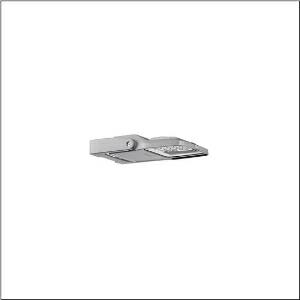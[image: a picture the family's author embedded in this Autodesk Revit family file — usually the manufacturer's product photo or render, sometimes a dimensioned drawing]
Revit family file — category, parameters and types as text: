
# Revit family: floodlight_fl_21_micro___pl64_5xa7761a2e2a_558a
name_source: partatom
category: Lighting Fixtures
units: mm (PartAtom-declared; Revit-internal decimal feet)

## family parameters
Cut with Voids When Loaded = No
Host = Face
Light Source = No
Part Type = Normal
Room Calculation Point = No
Round Connector Dimension = Use Diameter
Shared = No

## types (1)
- --- (1 x LED, 2870 lm, 23.1 W, 3000K)
    Apparent Load = 23 VA
    CIE Flux Codes = 28 80 98 100 100
    Color Rendering = 70
    Color Temperature = 3000K
    Default Elevation = 1800 mm
    Description = Floodlight FL 21 micro, floodlight, primary light control with lens, of PMMA, primary optical cover: protective disc, of toughened safety glass, transparent, light distribution: PL64, light emission: direct distribution, installation type: surface-mounted, LED, High Power LED, rated luminous flux: 2.870lm, luminous efficacy: 124lm/W, light colour: 730, colour temperature: 3000K, control gear: ECG iQ, control: optimised constant luminous flux control (CLO 2.0), Desk-Remote (wireless, voltage-free reading and setting of iQ features in the workshop via application-optimized NFC function/RFID function), Light-Fading, Smart-Wire, Night-Set, Lumen-Switch, Temp-Guard, Auto-Match, with terminal, 6-pole, mains connection: 220..240V, AC, 50/60Hz, start of lifetime: 23W, end of lifetime: 24W, reduction: 11W, luminaire housing, of diecast aluminium, powder-coated, Siteco® metallic grey (DB 702S), corrosivity category C5 according to DIN EN ISO 12944, design bracket, of diecast aluminium, powder-coated, Siteco® metallic grey (DB 702S), protection rating (complete): IP66, insulation class (complete): insulation class II (safety insulation), certification: CE, protection symbol: D, impact resistance: IK07, permissible operating ambient temperature: -40..+40°C, permissible operating ambient temperature for outdoor applications: -40..+50°C, standard: DIN EN 12944, packaging unit: 1 piece

Light Distribution: PL64
    Height = 65 mm
    Lamp = 1 x LED
    Lamp Light Flux = 2870 lm
    Lamp Power = 23.1 W
    Lamp count = 1
    Length = 312 mm
    Luminous efficacy = 124 lm/W
    Manufacturer = Siteco
    ModVariant = No
    Model = 5XA7761A2E2A
    Number of Poles = 1
    OnlyDefault = Yes
    Power Factor = 1
    Product Name = Floodlight FL 21 micro | PL64
    Product group = floodlight | pylon top
    ProductGroupID = 6101
    Protection Class = Protection class II
    Protection Degree = IP 66
    RLX_Detail_Level = 1
    RlxData = <blob elided: 97269 chars, md5=9edd14cb>
    Socket = socket
    Standby Power = 0 W
    System Light Flux = 2870 lm
    System Power = 23 W
    Type Comments = factory setting: luminous flux: 100 % | dim-lin: 254 | 455 mA
    Type Image = l_1006878.jpg
    URL = http://relux.com
    VarID = @adj_094455
    Voltage = 0 V
    Weight = 0.00 kg
    Width = 230 mm

## geometry (parser evidence)
native form markers: Blend x4, Sweep x13
no freeform markers — native parametric forms only
